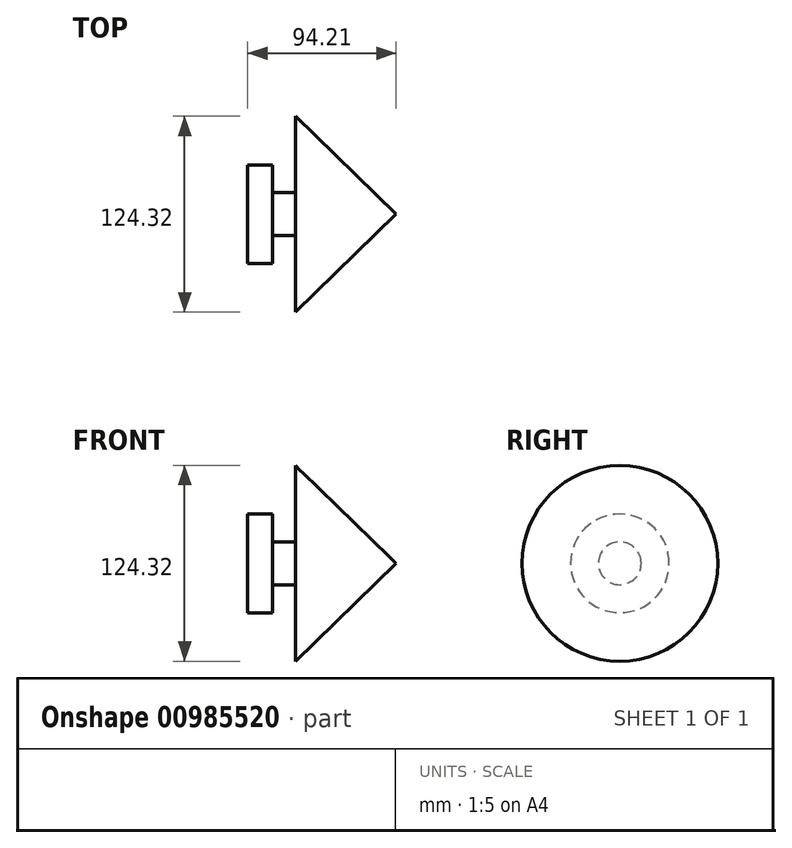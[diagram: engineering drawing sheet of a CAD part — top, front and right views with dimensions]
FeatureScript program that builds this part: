
annotation { "Feature Type Name" : "Feature", "Feature Type Description" : "" }
export const myFeature = defineFeature(function(context is Context, id is Id, definition is map)
    precondition{}
    {
        {
            var Q0;
            Q0=qCreatedBy(makeId("Front.planeOp"),FACE);
            var sketch = newSketch(context, id + "F0", { "sketchPlane" : qUnion([Q0])});
            skLineSegment(sketch, "E0", {"start": v(-47.17, 0) * mm, "end": v(-47.17, 31.34) * mm});
            skLineSegment(sketch, "E1", {"start": v(-47.17, 31.34) * mm, "end": v(-31.32, 31.34) * mm});
            skLineSegment(sketch, "E2", {"start": v(-31.32, 31.34) * mm, "end": v(-31.32, 13.59) * mm});
            skLineSegment(sketch, "E3", {"start": v(-31.32, 13.59) * mm, "end": v(-16.88, 13.59) * mm});
            skLineSegment(sketch, "E4", {"start": v(-16.88, 13.59) * mm, "end": v(-16.88, 62.16) * mm});
            skLineSegment(sketch, "E5", {"start": v(-16.88, 62.16) * mm, "end": v(47.04, 0) * mm});
            skLineSegment(sketch, "E6", {"start": v(47.04, 0) * mm, "end": v(-47.17, 0) * mm});
            skSolve(sketch);
        }
        {
            var Q0;
            Q0=makeQuery(id+"F0.imprint","IMPRINT",FACE,{"disambiguationData":[TD([[makeQuery(id+"F0.imprint","IMPRINT",EDGE,{"derivedFrom":sQuery(id+"F0.wireOp",EDGE,"E0")}),-1.0]])]});
            var Q1;
            Q1=sQuery(id+"F0.wireOp",EDGE,"E6");
            revolve(context, id + "F1", {"surfaceOperationType" : NewSurfaceOperationType.NEW, "entities" : qUnion([Q0]), "axis" : qUnion([Q1]), "revolveType" : RevolveType.FULL});
        }
    });
